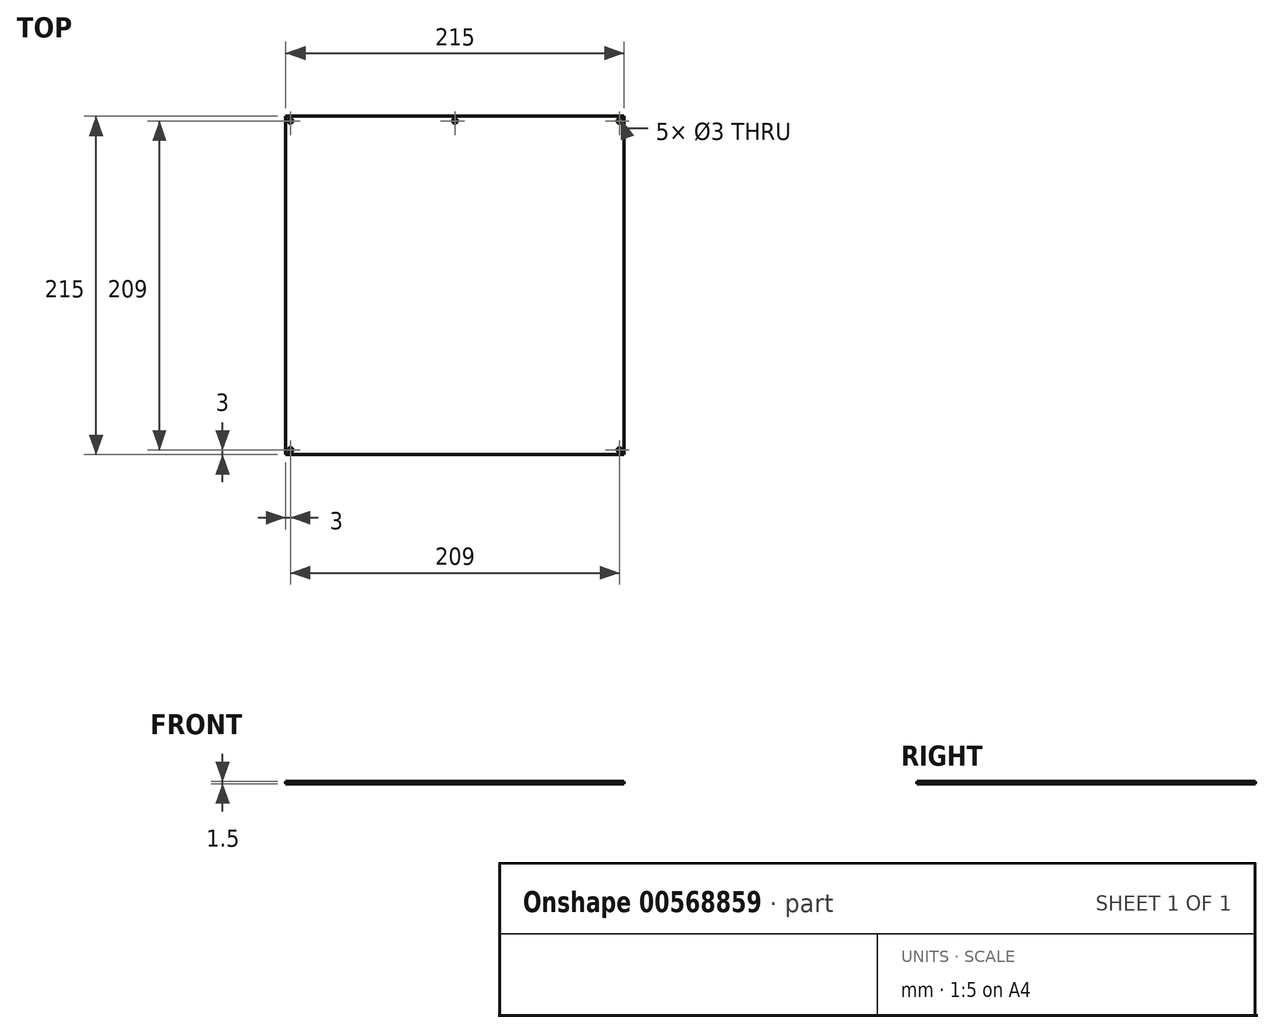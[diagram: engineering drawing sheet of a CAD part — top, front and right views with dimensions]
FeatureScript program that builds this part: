
annotation { "Feature Type Name" : "Feature", "Feature Type Description" : "" }
export const myFeature = defineFeature(function(context is Context, id is Id, definition is map)
    precondition{}
    {
        {
            var Q0;
            Q0=qCreatedBy(makeId("Top.planeOp"),FACE);
            var sketch = newSketch(context, id + "F0", { "sketchPlane" : qUnion([Q0])});
            skLineSegment(sketch, "E0.bottom", {"start": v(-107.5, 107.5) * mm, "end": v(107.5, 107.5) * mm});
            skLineSegment(sketch, "E0.top", {"start": v(-107.5, -107.5) * mm, "end": v(107.5, -107.5) * mm});
            skLineSegment(sketch, "E0.left", {"start": v(-107.5, 107.5) * mm, "end": v(-107.5, -107.5) * mm});
            skLineSegment(sketch, "E0.right", {"start": v(107.5, 107.5) * mm, "end": v(107.5, -107.5) * mm});
            skLineSegment(sketch, "E1", {"start": v(-107.5, 107.5) * mm, "end": v(107.5, -107.5) * mm, "construction": true});
            skLineSegment(sketch, "E2", {"start": v(-107.5, -107.5) * mm, "end": v(107.5, 107.5) * mm, "construction": true});
            skCircle(sketch, "E3", {"center": v(-104.5, 104.5) * mm, "radius": 1.5 * mm});
            skCircle(sketch, "E4", {"center": v(104.5, 104.5) * mm, "radius": 1.5 * mm});
            skCircle(sketch, "E5", {"center": v(104.5, -104.5) * mm, "radius": 1.5 * mm});
            skCircle(sketch, "E6", {"center": v(-104.5, -104.5) * mm, "radius": 1.5 * mm});
            skCircle(sketch, "E7", {"center": v(0, 104.5) * mm, "radius": 1.5 * mm});
            skSolve(sketch);
        }
        {
            var Q0;
            Q0 = qSketchRegion(id + "F0", true);
            extrude(context, id + "F1", {"entities" : qUnion([Q0]), "depth" : 1.5 * mm, "offsetDistance" : 25 * mm});
        }
    });
